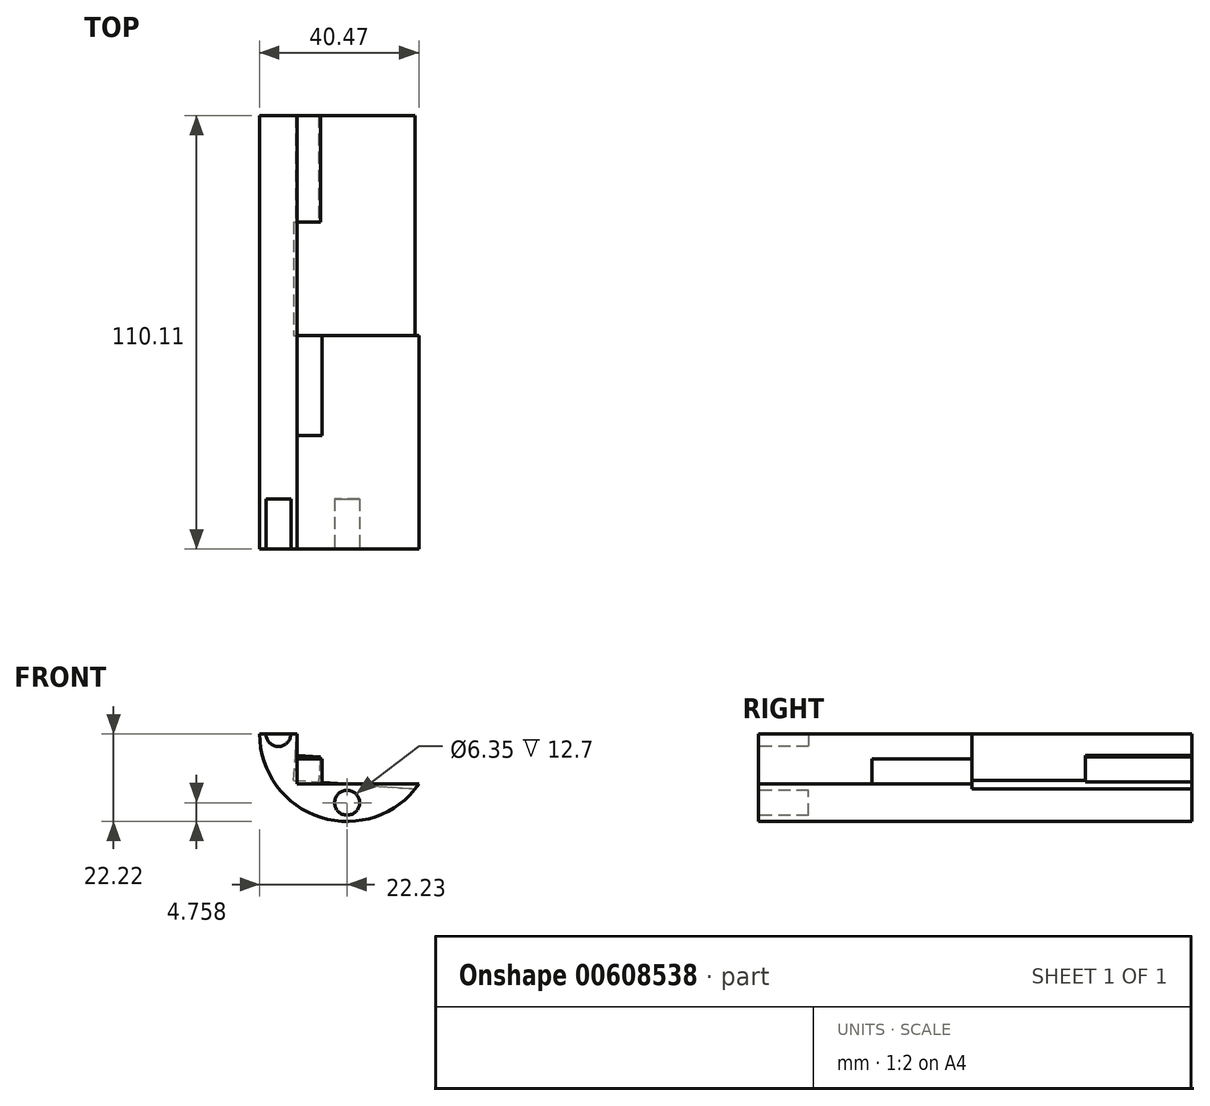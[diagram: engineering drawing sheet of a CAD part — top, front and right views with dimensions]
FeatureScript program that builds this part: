
annotation { "Feature Type Name" : "Feature", "Feature Type Description" : "" }
export const myFeature = defineFeature(function(context is Context, id is Id, definition is map)
    precondition{}
    {
        {
            var Q0;
            Q0=qCreatedBy(makeId("Front.planeOp"),FACE);
            var sketch = newSketch(context, id + "F0", { "sketchPlane" : qUnion([Q0])});
            skLineSegment(sketch, "E0", {"start": v(-12.7, -12.7) * mm, "end": v(-12.7, 18.24) * mm});
            skLineSegment(sketch, "E1", {"start": v(-12.7, -12.7) * mm, "end": v(18.24, -12.7) * mm});
            skArc(sketch, "E2", {"start": v(-12.7, 18.24) * mm, "mid": v(-15.72, -15.72) * mm, "end": v(18.24, -12.7) * mm});
            skSolve(sketch);
        }
        {
            var Q0;
            Q0=makeQuery(id+"F0.imprint","IMPRINT",FACE,{"disambiguationData":[TD([[makeQuery(id+"F0.imprint","IMPRINT",EDGE,{"derivedFrom":sQuery(id+"F0.wireOp",EDGE,"E0")}),1.0]])]});
            extrude(context, id + "F1", {"entities" : qUnion([Q0]), "oppositeDirection" : true, "depth" : 28.83 * mm, "offsetDistance" : 25.4 * mm});
        }
        {
            var Q0;
            Q0=makeQuery(id+"F1.opExtrude","CAP_FACE",FACE,{"disambiguationData":[OSD([sQuery(id+"F0.wireOp",EDGE,"E0"),sQuery(id+"F0.wireOp",EDGE,"E1"),sQuery(id+"F0.wireOp",EDGE,"E2")])],"isStart":false});
            var sketch = newSketch(context, id + "F2", { "sketchPlane" : qUnion([Q0])});
            skLineSegment(sketch, "E3", {"start": v(12.7, -12.7) * mm, "end": v(12.7, -6.35) * mm});
            skLineSegment(sketch, "E4", {"start": v(12.7, -6.35) * mm, "end": v(6.35, -6.35) * mm});
            skLineSegment(sketch, "E5", {"start": v(6.35, -6.35) * mm, "end": v(6.35, -12.7) * mm});
            skSolve(sketch);
        }
        {
            var Q0;
            {var subQ2=sQuery(id+"F2.wireOp",EDGE,"E3");Q0=makeQuery(id+"F2.imprint","IMPRINT",FACE,{"disambiguationData":[TD([[makeQuery(id+"F2.imprint","IMPRINT",EDGE,{"derivedFrom":subQ2}),-1.0]])]});}
            var Q1;
            {var subQ0=sQuery(id+"F2.wireOp",EDGE,"E3");Q1=makeQuery(id+"F2.imprint","IMPRINT",FACE,{"disambiguationData":[TD([[makeQuery(id+"F2.imprint","IMPRINT",EDGE,{"derivedFrom":subQ0}),1.0]])]});}
            extrude(context, id + "F3", {"entities" : qUnion([Q0, Q1]), "operationType" : NewBodyOperationType.ADD, "depth" : 25.4 * mm, "offsetDistance" : 25.4 * mm});
        }
        {
            var Q0;
            Q0=makeQuery(id+"F3.opExtrude","CAP_FACE",FACE,{"disambiguationData":[OSD([sQuery(id+"F0.wireOp",EDGE,"E0"),sQuery(id+"F0.wireOp",EDGE,"E1"),sQuery(id+"F0.wireOp",EDGE,"E2"),sQuery(id+"F2.wireOp",EDGE,"E4"),sQuery(id+"F2.wireOp",EDGE,"E5")])],"isStart":false});
            var sketch = newSketch(context, id + "F4", { "sketchPlane" : qUnion([Q0])});
            skArc(sketch, "E6", {"start": v(-17.3, -13.94) * mm, "mid": v(16.77, -14.58) * mm, "end": v(11.4, 19.08) * mm});
            skLineSegment(sketch, "E7", {"start": v(13.55, -11.78) * mm, "end": v(11.4, 19.08) * mm});
            skLineSegment(sketch, "E8", {"start": v(13.55, -11.78) * mm, "end": v(-17.3, -13.94) * mm});
            skSolve(sketch);
        }
        {
            var Q0;
            {var subQ0=sQuery(id+"F4.wireOp",EDGE,"E8");var subQ5=sQuery(id+"F4.wireOp",EDGE,"E7");var subQ6=makeQuery(id+"F4.imprint","INTERSECT",VERTEX,{"derivedFrom":[subQ5,subQ0]});Q0=makeQuery(id+"F4.imprint","IMPRINT",FACE,{"disambiguationData":[TD([[makeQuery(id+"F4.imprint","IMPRINT",EDGE,{"disambiguationData":[TD([[subQ6,-1.0]])],"derivedFrom":subQ5}),-1.0]])]});}
            var Q1;
            {var subQ0=sQuery(id+"F4.wireOp",EDGE,"E6");var subQ3=sQuery(id+"F4.wireOp",EDGE,"E7");var subQ4=makeQuery(id+"F4.imprint","INTERSECT",VERTEX,{"derivedFrom":[subQ0,subQ3]});Q1=makeQuery(id+"F4.imprint","IMPRINT",FACE,{"disambiguationData":[TD([[makeQuery(id+"F4.imprint","IMPRINT",EDGE,{"disambiguationData":[TD([[subQ4,1.0]])],"derivedFrom":subQ0}),1.0]])]});}
            var Q2;
            {var subQ0=sQuery(id+"F4.wireOp",EDGE,"E8");var subQ1=makeQuery(id+"F3.opExtrude","CAP_EDGE",EDGE,{"disambiguationData":[OSD([sQuery(id+"F2.wireOp",EDGE,"E5")])],"isStart":false});var subQ2=makeQuery(id+"F4.imprint","INTERSECT",VERTEX,{"derivedFrom":[subQ1,subQ0]});Q2=makeQuery(id+"F4.imprint","IMPRINT",FACE,{"disambiguationData":[TD([[makeQuery(id+"F4.imprint","IMPRINT",EDGE,{"disambiguationData":[TD([[subQ2,-1.0]])],"derivedFrom":subQ0}),1.0]])]});}
            extrude(context, id + "F5", {"entities" : qUnion([Q0, Q1, Q2]), "operationType" : NewBodyOperationType.ADD, "depth" : 28.83 * mm, "offsetDistance" : 25.4 * mm});
        }
        {
            var Q0;
            Q0=makeQuery(id+"F5.opExtrude","CAP_FACE",FACE,{"disambiguationData":[OSD([sQuery(id+"F4.wireOp",EDGE,"E6"),sQuery(id+"F4.wireOp",EDGE,"E7"),sQuery(id+"F4.wireOp",EDGE,"E8")])],"isStart":false});
            var sketch = newSketch(context, id + "F6", { "sketchPlane" : qUnion([Q0])});
            skLineSegment(sketch, "E9", {"start": v(13.55, -11.78) * mm, "end": v(13.11, -5.45) * mm});
            skLineSegment(sketch, "E10", {"start": v(13.11, -5.45) * mm, "end": v(6.78, -5.9) * mm});
            skLineSegment(sketch, "E11", {"start": v(6.78, -5.9) * mm, "end": v(7.22, -12.23) * mm});
            skSolve(sketch);
        }
        {
            var Q0;
            {var subQ2=sQuery(id+"F6.wireOp",EDGE,"E9");Q0=makeQuery(id+"F6.imprint","IMPRINT",FACE,{"disambiguationData":[TD([[makeQuery(id+"F6.imprint","IMPRINT",EDGE,{"derivedFrom":subQ2}),-1.0]])]});}
            var Q1;
            {var subQ0=sQuery(id+"F6.wireOp",EDGE,"E9");Q1=makeQuery(id+"F6.imprint","IMPRINT",FACE,{"disambiguationData":[TD([[makeQuery(id+"F6.imprint","IMPRINT",EDGE,{"derivedFrom":subQ0}),1.0]])]});}
            extrude(context, id + "F7", {"entities" : qUnion([Q0, Q1]), "operationType" : NewBodyOperationType.ADD, "depth" : 27.05 * mm, "offsetDistance" : 25.4 * mm});
        }
        {
            var Q0;
            Q0=makeQuery(id+"F1.opExtrude","CAP_FACE",FACE,{"disambiguationData":[OSD([sQuery(id+"F0.wireOp",EDGE,"E0"),sQuery(id+"F0.wireOp",EDGE,"E1"),sQuery(id+"F0.wireOp",EDGE,"E2")])],"isStart":true});
            var sketch = newSketch(context, id + "F8", { "sketchPlane" : qUnion([Q0])});
            skCircle(sketch, "E12", {"center": v(-17.46, 0) * mm, "radius": 3.18 * mm});
            skCircle(sketch, "E13", {"center": v(0, -17.46) * mm, "radius": 3.18 * mm});
            skSolve(sketch);
        }
        {
            var Q0;
            Q0=makeQuery(id+"F8.imprint","IMPRINT",FACE,{"disambiguationData":[TD([[makeQuery(id+"F8.imprint","IMPRINT",EDGE,{"derivedFrom":sQuery(id+"F8.wireOp",EDGE,"E12")}),1.0]])]});
            var Q1;
            Q1=makeQuery(id+"F8.imprint","IMPRINT",FACE,{"disambiguationData":[TD([[makeQuery(id+"F8.imprint","IMPRINT",EDGE,{"derivedFrom":sQuery(id+"F8.wireOp",EDGE,"E13")}),1.0]])]});
            extrude(context, id + "F9", {"entities" : qUnion([Q0, Q1]), "operationType" : NewBodyOperationType.REMOVE, "oppositeDirection" : true, "depth" : 12.7 * mm, "offsetDistance" : 25.4 * mm});
        }
        {
            var Q0;
            Q0=qCreatedBy(makeId("Front.planeOp"),FACE);
            var sketch = newSketch(context, id + "F10", { "sketchPlane" : qUnion([Q0])});
            skLineSegment(sketch, "E14.bottom", {"start": v(-41.76, 32.54) * mm, "end": v(28.85, 32.54) * mm});
            skLineSegment(sketch, "E14.top", {"start": v(-41.76, 0) * mm, "end": v(28.85, 0) * mm});
            skLineSegment(sketch, "E14.left", {"start": v(-41.76, 32.54) * mm, "end": v(-41.76, 0) * mm});
            skLineSegment(sketch, "E14.right", {"start": v(28.85, 32.54) * mm, "end": v(28.85, 0) * mm});
            skSolve(sketch);
        }
        {
            var Q0;
            Q0=makeQuery(id+"F10.imprint","IMPRINT",FACE,{"disambiguationData":[TD([[makeQuery(id+"F10.imprint","IMPRINT",EDGE,{"derivedFrom":sQuery(id+"F10.wireOp",EDGE,"E14.bottom")}),-1.0]])]});
            extrude(context, id + "F11", {"entities" : qUnion([Q0]), "operationType" : NewBodyOperationType.REMOVE, "endBound" : BoundingType.THROUGH_ALL, "oppositeDirection" : true, "depth" : 25.4 * mm, "offsetDistance" : 25.4 * mm});
        }
    });
